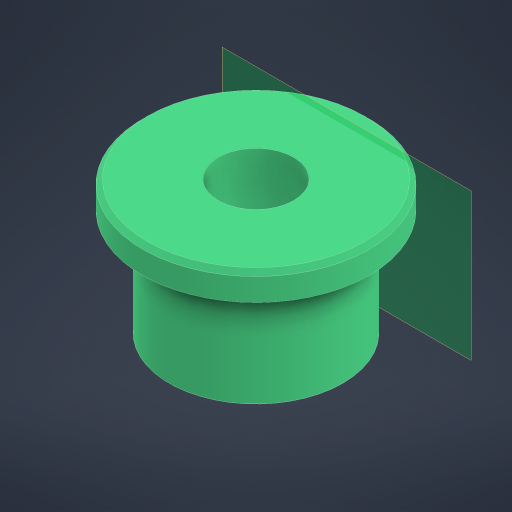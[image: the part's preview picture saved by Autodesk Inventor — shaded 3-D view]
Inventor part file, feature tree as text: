
AUTODESK INVENTOR PART (.ipt)
format: ipt  version: 2024 (Build 280153000, 153)  size: 225,280 bytes
history: native  units: mm
features: other x8, extrude x5, sketch x5, reference x2, chamfer x1
ambient origin geometry x8: Origin, YZ Plane, XZ Plane, XY Plane, X Axis, Y Axis, Z Axis, Center Point
bodies: Body1 (feature_tree)
feature tree (21):
  other  "Твердое тело1"
  other  "РабПлоскость1"
  extrude  "Выдавливание1"  Depth=11.75mm TaperAngle=0.0deg
  extrude  "Выдавливание2"  Depth=3.0mm TaperAngle=0.0deg
  chamfer  "Фаска1"  Distance=0.5mm Angle=45.0deg
  extrude  "Выдавливание8"  Depth=12.0mm
  extrude  "Выдавливание9"  Depth=5.0mm TaperAngle=0.0deg
  other  "РабПлоскость3"
  extrude  "Выдавливание12"  Depth=8.3mm
  sketch  "Эскиз1"
  reference  "Ссылка1"
  sketch  "Эскиз2"
  reference  "Ссылка2"
  sketch  "Эскиз8"
  sketch  "Эскиз9"
  sketch  "Эскиз12"
  parser-record x2  (decoder bookkeeping rows leaked as tree rows — omitted from the tree; the rows remain in map.json)
  other  "motor_assembly_S.iam"
  other  "lower_arm:1"
  other  "motor_assembly.iam"
note: 2 file-system paths scrubbed to <path> (originals preserved in map.json)
